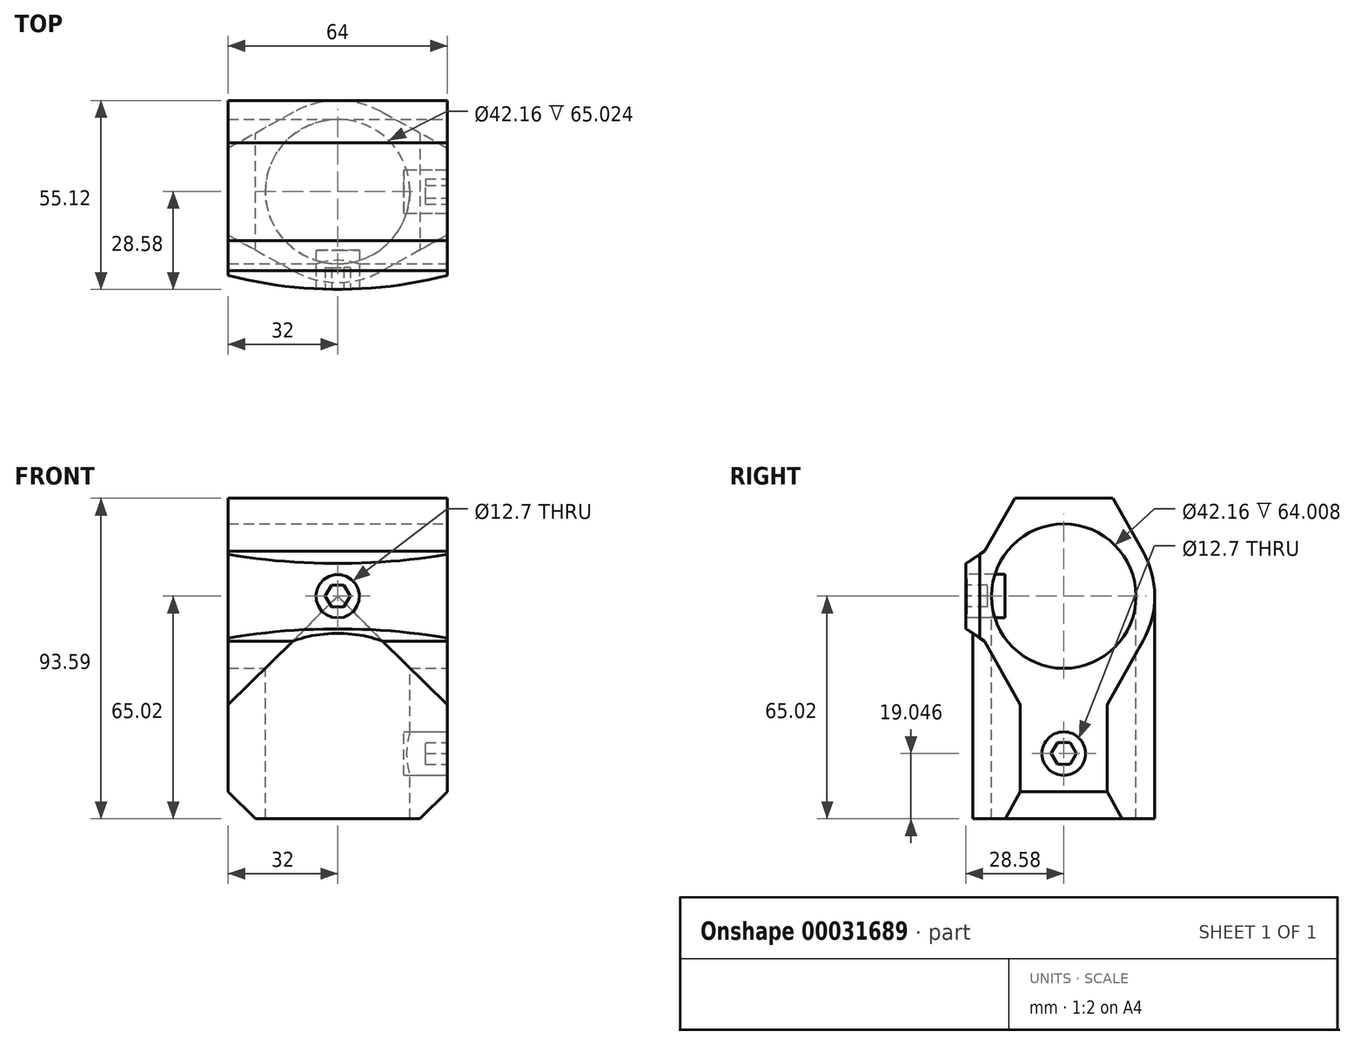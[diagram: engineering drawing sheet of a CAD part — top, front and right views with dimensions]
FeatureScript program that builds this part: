
annotation { "Feature Type Name" : "Feature", "Feature Type Description" : "" }
export const myFeature = defineFeature(function(context is Context, id is Id, definition is map)
    precondition{}
    {
        {
            var Q0;
            Q0=qCreatedBy(makeId("Top.planeOp"),FACE);
            var sketch = newSketch(context, id + "F0", { "sketchPlane" : qUnion([Q0])});
            skCircle(sketch, "E0", {"center": v(0, 0) * mm, "radius": 21.08 * mm});
            skCircle(sketch, "E1", {"center": v(0, 0) * mm, "radius": 26.54 * mm});
            skLineSegment(sketch, "E2.rect.bottom", {"start": v(-32, -12.7) * mm, "end": v(32, -12.7) * mm});
            skLineSegment(sketch, "E2.rect.top", {"start": v(-32, 12.7) * mm, "end": v(32, 12.7) * mm});
            skLineSegment(sketch, "E2.rect.left", {"start": v(-32, -12.7) * mm, "end": v(-32, 12.7) * mm});
            skLineSegment(sketch, "E2.rect.right", {"start": v(32, -12.7) * mm, "end": v(32, 12.7) * mm});
            skLineSegment(sketch, "E3", {"start": v(-32, -12.7) * mm, "end": v(-12.78, -23.26) * mm});
            skLineSegment(sketch, "E4", {"start": v(-32, 12.7) * mm, "end": v(-12.78, 23.26) * mm});
            skLineSegment(sketch, "E5", {"start": v(32, 12.7) * mm, "end": v(12.78, 23.26) * mm});
            skLineSegment(sketch, "E6", {"start": v(32, -12.7) * mm, "end": v(12.78, -23.26) * mm});
            skSolve(sketch);
        }
        {
            var Q0;
            {var subQ0=sQuery(id+"F0.wireOp",EDGE,"E2.rect.top");var subQ3=sQuery(id+"F0.wireOp",EDGE,"E0");var subQ4=makeQuery(id+"F0.imprint","INTERSECT",VERTEX,{"disambiguationData":[OD(0.0)],"derivedFrom":[subQ3,subQ0]});Q0=makeQuery(id+"F0.imprint","IMPRINT",FACE,{"disambiguationData":[TD([[makeQuery(id+"F0.imprint","IMPRINT",EDGE,{"disambiguationData":[TD([[subQ4,-1.0]])],"derivedFrom":subQ3}),-1.0]])]});}
            var Q1;
            {var subQ0=sQuery(id+"F0.wireOp",EDGE,"E3");Q1=makeQuery(id+"F0.imprint","IMPRINT",FACE,{"disambiguationData":[TD([[makeQuery(id+"F0.imprint","IMPRINT",EDGE,{"derivedFrom":subQ0}),1.0]])]});}
            var Q2;
            {var subQ0=sQuery(id+"F0.wireOp",EDGE,"E2.rect.bottom");var subQ3=sQuery(id+"F0.wireOp",EDGE,"E0");var subQ4=makeQuery(id+"F0.imprint","INTERSECT",VERTEX,{"disambiguationData":[OD(0.0)],"derivedFrom":[subQ3,subQ0]});Q2=makeQuery(id+"F0.imprint","IMPRINT",FACE,{"disambiguationData":[TD([[makeQuery(id+"F0.imprint","IMPRINT",EDGE,{"disambiguationData":[TD([[subQ4,-1.0]])],"derivedFrom":subQ3}),-1.0]])]});}
            var Q3;
            {var subQ0=sQuery(id+"F0.wireOp",EDGE,"E6");Q3=makeQuery(id+"F0.imprint","IMPRINT",FACE,{"disambiguationData":[TD([[makeQuery(id+"F0.imprint","IMPRINT",EDGE,{"derivedFrom":subQ0}),-1.0]])]});}
            var Q4;
            {var subQ0=sQuery(id+"F0.wireOp",EDGE,"E2.rect.right");Q4=makeQuery(id+"F0.imprint","IMPRINT",FACE,{"disambiguationData":[TD([[makeQuery(id+"F0.imprint","IMPRINT",EDGE,{"derivedFrom":subQ0}),1.0]])]});}
            var Q5;
            {var subQ0=sQuery(id+"F0.wireOp",EDGE,"E2.rect.top");var subQ3=sQuery(id+"F0.wireOp",EDGE,"E0");var subQ4=makeQuery(id+"F0.imprint","INTERSECT",VERTEX,{"disambiguationData":[OD(1.0)],"derivedFrom":[subQ3,subQ0]});Q5=makeQuery(id+"F0.imprint","IMPRINT",FACE,{"disambiguationData":[TD([[makeQuery(id+"F0.imprint","IMPRINT",EDGE,{"disambiguationData":[TD([[subQ4,1.0]])],"derivedFrom":subQ3}),-1.0]])]});}
            var Q6;
            {var subQ0=sQuery(id+"F0.wireOp",EDGE,"E5");Q6=makeQuery(id+"F0.imprint","IMPRINT",FACE,{"disambiguationData":[TD([[makeQuery(id+"F0.imprint","IMPRINT",EDGE,{"derivedFrom":subQ0}),1.0]])]});}
            var Q7;
            {var subQ0=sQuery(id+"F0.wireOp",EDGE,"E2.rect.top");var subQ3=sQuery(id+"F0.wireOp",EDGE,"E0");var subQ6=makeQuery(id+"F0.imprint","INTERSECT",VERTEX,{"disambiguationData":[OD(0.0)],"derivedFrom":[subQ3,subQ0]});Q7=makeQuery(id+"F0.imprint","IMPRINT",FACE,{"disambiguationData":[TD([[makeQuery(id+"F0.imprint","IMPRINT",EDGE,{"disambiguationData":[TD([[subQ6,1.0]])],"derivedFrom":subQ3}),-1.0]])]});}
            var Q8;
            {var subQ0=sQuery(id+"F0.wireOp",EDGE,"E4");Q8=makeQuery(id+"F0.imprint","IMPRINT",FACE,{"disambiguationData":[TD([[makeQuery(id+"F0.imprint","IMPRINT",EDGE,{"derivedFrom":subQ0}),-1.0]])]});}
            var Q9;
            {var subQ0=sQuery(id+"F0.wireOp",EDGE,"E2.rect.left");Q9=makeQuery(id+"F0.imprint","IMPRINT",FACE,{"disambiguationData":[TD([[makeQuery(id+"F0.imprint","IMPRINT",EDGE,{"derivedFrom":subQ0}),-1.0]])]});}
            var Q10;
            {var subQ0=sQuery(id+"F0.wireOp",EDGE,"E2.rect.top");var subQ1=sQuery(id+"F0.wireOp",EDGE,"E0");var subQ3=makeQuery(id+"F0.imprint","INTERSECT",VERTEX,{"disambiguationData":[OD(0.0)],"derivedFrom":[subQ1,subQ0]});Q10=makeQuery(id+"F0.imprint","IMPRINT",FACE,{"disambiguationData":[TD([[makeQuery(id+"F0.imprint","IMPRINT",EDGE,{"disambiguationData":[TD([[subQ3,1.0]])],"derivedFrom":subQ1}),1.0]])]});}
            var Q11;
            {var subQ1=sQuery(id+"F0.wireOp",EDGE,"E0");var subQ4=sQuery(id+"F0.wireOp",EDGE,"E2.rect.top");var subQ6=makeQuery(id+"F0.imprint","INTERSECT",VERTEX,{"disambiguationData":[OD(0.0)],"derivedFrom":[subQ1,subQ4]});Q11=makeQuery(id+"F0.imprint","IMPRINT",FACE,{"disambiguationData":[TD([[makeQuery(id+"F0.imprint","IMPRINT",EDGE,{"disambiguationData":[TD([[subQ6,-1.0]])],"derivedFrom":subQ1}),1.0]])]});}
            var Q12;
            {var subQ0=sQuery(id+"F0.wireOp",EDGE,"E2.rect.bottom");var subQ1=sQuery(id+"F0.wireOp",EDGE,"E0");var subQ3=makeQuery(id+"F0.imprint","INTERSECT",VERTEX,{"disambiguationData":[OD(0.0)],"derivedFrom":[subQ1,subQ0]});Q12=makeQuery(id+"F0.imprint","IMPRINT",FACE,{"disambiguationData":[TD([[makeQuery(id+"F0.imprint","IMPRINT",EDGE,{"disambiguationData":[TD([[subQ3,-1.0]])],"derivedFrom":subQ1}),1.0]])]});}
            extrude(context, id + "F1", {"entities" : qUnion([Q0, Q1, Q2, Q3, Q4, Q5, Q6, Q7, Q8, Q9, Q10, Q11, Q12]), "oppositeDirection" : true, "depth" : 65.02 * mm});
        }
        {
            var Q0;
            Q0=qCreatedBy(makeId("Right.planeOp"),FACE);
            var sketch = newSketch(context, id + "F2", { "sketchPlane" : qUnion([Q0])});
            skCircle(sketch, "E7", {"center": v(0, 0) * mm, "radius": 21.08 * mm});
            skCircle(sketch, "E8", {"center": v(0, 0) * mm, "radius": 26.54 * mm});
            skLineSegment(sketch, "E9", {"start": v(-12.7, -31.75) * mm, "end": v(12.7, -31.75) * mm});
            skLineSegment(sketch, "E10", {"start": v(12.7, -31.75) * mm, "end": v(23.19, -12.91) * mm});
            skLineSegment(sketch, "E11", {"start": v(-12.7, -31.75) * mm, "end": v(-23.19, -12.91) * mm});
            skLineSegment(sketch, "E12", {"start": v(0, 28.58) * mm, "end": v(-14.29, 28.58) * mm});
            skLineSegment(sketch, "E13", {"start": v(-14.29, 28.58) * mm, "end": v(-23.07, 13.12) * mm});
            skLineSegment(sketch, "E14.MirrorCS", {"start": v(0, 28.58) * mm, "end": v(14.29, 28.58) * mm});
            skLineSegment(sketch, "E15.MirrorCS", {"start": v(14.29, 28.58) * mm, "end": v(23.07, 13.12) * mm});
            skLineSegment(sketch, "E16", {"start": v(-28.58, 0) * mm, "end": v(-28.58, 9.52) * mm});
            skLineSegment(sketch, "E17", {"start": v(-28.58, 9.53) * mm, "end": v(-23.07, 13.12) * mm});
            skLineSegment(sketch, "E18.MirrorCS", {"start": v(-28.58, 0) * mm, "end": v(-28.58, -9.52) * mm});
            skLineSegment(sketch, "E19.MirrorCS", {"start": v(-28.58, -9.53) * mm, "end": v(-23.07, -13.12) * mm});
            skSolve(sketch);
        }
        {
            var Q0;
            Q0=makeQuery(id+"F2.imprint","IMPRINT",FACE,{"disambiguationData":[TD([[makeQuery(id+"F2.imprint","IMPRINT",EDGE,{"derivedFrom":sQuery(id+"F2.wireOp",EDGE,"E12")}),1.0]])]});
            var Q1;
            Q1=makeQuery(id+"F2.imprint","IMPRINT",FACE,{"disambiguationData":[TD([[makeQuery(id+"F2.imprint","IMPRINT",EDGE,{"derivedFrom":sQuery(id+"F2.wireOp",EDGE,"E7")}),-1.0]])]});
            var Q2;
            Q2=makeQuery(id+"F2.imprint","IMPRINT",FACE,{"disambiguationData":[TD([[makeQuery(id+"F2.imprint","IMPRINT",EDGE,{"derivedFrom":sQuery(id+"F2.wireOp",EDGE,"E9")}),1.0]])]});
            var Q3;
            Q3=makeQuery(id+"F2.imprint","IMPRINT",FACE,{"disambiguationData":[TD([[makeQuery(id+"F2.imprint","IMPRINT",EDGE,{"derivedFrom":sQuery(id+"F2.wireOp",EDGE,"E7")}),1.0]])]});
            var Q4;
            {var subQ1=sQuery(id+"F2.wireOp",EDGE,"E11");var subQ3=sQuery(id+"F2.wireOp",EDGE,"E8");var subQ5=makeQuery(id+"F2.imprint","INTERSECT",VERTEX,{"derivedFrom":[subQ3,subQ1]});Q4=makeQuery(id+"F2.imprint","IMPRINT",FACE,{"disambiguationData":[TD([[makeQuery(id+"F2.imprint","IMPRINT",EDGE,{"disambiguationData":[TD([[subQ5,-1.0]])],"derivedFrom":subQ3}),-1.0]])]});}
            var Q5;
            Q5=makeQuery(id+"F2.imprint","IMPRINT",FACE,{"disambiguationData":[TD([[makeQuery(id+"F2.imprint","IMPRINT",EDGE,{"derivedFrom":sQuery(id+"F2.wireOp",EDGE,"E16")}),-1.0]])]});
            var Q6;
            Q6=makeQuery(id+"F1.opExtrude","SWEPT_FACE",FACE,{"disambiguationData":[OSD([sQuery(id+"F0.wireOp",EDGE,"E2.rect.right")])]});
            var Q7;
            Q7=makeQuery(id+"F1.opExtrude","SWEPT_FACE",FACE,{"disambiguationData":[OSD([sQuery(id+"F0.wireOp",EDGE,"E2.rect.left")])]});
            extrude(context, id + "F3", {"entities" : qUnion([Q0, Q1, Q2, Q3, Q4, Q5]), "operationType" : NewBodyOperationType.ADD, "endBound" : BoundingType.UP_TO_SURFACE, "endBoundEntityFace" : qUnion([Q6]), "depth" : 25.4 * mm, "hasSecondDirection" : true, "secondDirectionBound" : SecondDirectionBoundingType.UP_TO_SURFACE, "secondDirectionOppositeDirection" : true, "secondDirectionBoundEntityFace" : qUnion([Q7]), "secondDirectionDepth" : 25.4 * mm});
        }
        {
            var Q0;
            Q0=makeQuery(id+"F2.imprint","IMPRINT",FACE,{"disambiguationData":[TD([[makeQuery(id+"F2.imprint","IMPRINT",EDGE,{"derivedFrom":sQuery(id+"F2.wireOp",EDGE,"E7")}),1.0]])]});
            extrude(context, id + "F4", {"entities" : qUnion([Q0]), "operationType" : NewBodyOperationType.REMOVE, "endBound" : BoundingType.THROUGH_ALL, "oppositeDirection" : true, "depth" : 25.4 * mm, "hasSecondDirection" : true, "secondDirectionBound" : SecondDirectionBoundingType.THROUGH_ALL, "secondDirectionOppositeDirection" : false, "secondDirectionDepth" : 25.4 * mm});
        }
        {
            var Q0;
            {var subQ0=sQuery(id+"F0.wireOp",EDGE,"E2.rect.bottom");var subQ1=sQuery(id+"F0.wireOp",EDGE,"E0");var subQ3=makeQuery(id+"F0.imprint","INTERSECT",VERTEX,{"disambiguationData":[OD(0.0)],"derivedFrom":[subQ1,subQ0]});Q0=makeQuery(id+"F0.imprint","IMPRINT",FACE,{"disambiguationData":[TD([[makeQuery(id+"F0.imprint","IMPRINT",EDGE,{"disambiguationData":[TD([[subQ3,-1.0]])],"derivedFrom":subQ1}),1.0]])]});}
            var Q1;
            {var subQ1=sQuery(id+"F0.wireOp",EDGE,"E0");var subQ4=sQuery(id+"F0.wireOp",EDGE,"E2.rect.top");var subQ6=makeQuery(id+"F0.imprint","INTERSECT",VERTEX,{"disambiguationData":[OD(0.0)],"derivedFrom":[subQ1,subQ4]});Q1=makeQuery(id+"F0.imprint","IMPRINT",FACE,{"disambiguationData":[TD([[makeQuery(id+"F0.imprint","IMPRINT",EDGE,{"disambiguationData":[TD([[subQ6,-1.0]])],"derivedFrom":subQ1}),1.0]])]});}
            var Q2;
            {var subQ0=sQuery(id+"F0.wireOp",EDGE,"E2.rect.top");var subQ1=sQuery(id+"F0.wireOp",EDGE,"E0");var subQ3=makeQuery(id+"F0.imprint","INTERSECT",VERTEX,{"disambiguationData":[OD(0.0)],"derivedFrom":[subQ1,subQ0]});Q2=makeQuery(id+"F0.imprint","IMPRINT",FACE,{"disambiguationData":[TD([[makeQuery(id+"F0.imprint","IMPRINT",EDGE,{"disambiguationData":[TD([[subQ3,1.0]])],"derivedFrom":subQ1}),1.0]])]});}
            extrude(context, id + "F5", {"entities" : qUnion([Q0, Q1, Q2]), "operationType" : NewBodyOperationType.REMOVE, "endBound" : BoundingType.THROUGH_ALL, "oppositeDirection" : true, "depth" : 25.4 * mm});
        }
        {
            var Q0;
            Q0=makeQuery(id+"F1.opExtrude","CAP_EDGE",EDGE,{"disambiguationData":[OSD([sQuery(id+"F0.wireOp",EDGE,"E2.rect.right")])],"isStart":false});
            var Q1;
            Q1=makeQuery(id+"F1.opExtrude","CAP_EDGE",EDGE,{"disambiguationData":[OSD([sQuery(id+"F0.wireOp",EDGE,"E2.rect.left")])],"isStart":false});
            chamfer(context, id + "F6", {"entities" : qUnion([Q0, Q1]), "width" : 7.94 * mm, "tangentPropagation" : true});
        }
        {
            var Q0;
            Q0=makeQuery(id+"F3.boolean.opBoolean","MERGE",FACE,{"derivedFrom":[makeQuery(id+"F1.opExtrude","SWEPT_FACE",FACE,{"disambiguationData":[OSD([sQuery(id+"F0.wireOp",EDGE,"E2.rect.right")])]}),makeQuery(id+"F3.opExtrude","CAP_FACE",FACE,{"disambiguationData":[OSD([sQuery(id+"F2.wireOp",EDGE,"E8"),sQuery(id+"F2.wireOp",EDGE,"E9"),sQuery(id+"F2.wireOp",EDGE,"E10"),sQuery(id+"F2.wireOp",EDGE,"E11"),sQuery(id+"F2.wireOp",EDGE,"E12"),sQuery(id+"F2.wireOp",EDGE,"E13"),sQuery(id+"F2.wireOp",EDGE,"E14.MirrorCS"),sQuery(id+"F2.wireOp",EDGE,"E15.MirrorCS"),sQuery(id+"F2.wireOp",EDGE,"E16"),sQuery(id+"F2.wireOp",EDGE,"E17"),sQuery(id+"F2.wireOp",EDGE,"E18.MirrorCS"),sQuery(id+"F2.wireOp",EDGE,"E19.MirrorCS")])],"isStart":false})]});
            var sketch = newSketch(context, id + "F7", { "sketchPlane" : qUnion([Q0])});
            skCircle(sketch, "E20", {"center": v(0, -45.97) * mm, "radius": 6.35 * mm});
            skCircle(sketch, "E21.cCircle", {"center": v(0, -45.97) * mm, "radius": 3.18 * mm, "construction": true});
            skLineSegment(sketch, "E21.0", {"start": v(-1.83, -42.8) * mm, "end": v(1.83, -42.8) * mm});
            skLineSegment(sketch, "E21.1", {"start": v(1.83, -42.8) * mm, "end": v(3.67, -45.97) * mm});
            skLineSegment(sketch, "E21.2", {"start": v(3.67, -45.97) * mm, "end": v(1.83, -49.15) * mm});
            skLineSegment(sketch, "E21.3", {"start": v(1.83, -49.15) * mm, "end": v(-1.83, -49.15) * mm});
            skLineSegment(sketch, "E21.4", {"start": v(-1.83, -49.15) * mm, "end": v(-3.67, -45.97) * mm});
            skLineSegment(sketch, "E21.5", {"start": v(-3.67, -45.97) * mm, "end": v(-1.83, -42.8) * mm});
            skPoint(sketch, "E21.0.midPoint", {"position": v(0, -42.8) * mm});
            skSolve(sketch);
        }
        {
            var Q0;
            Q0=makeQuery(id+"F7.imprint","IMPRINT",FACE,{"disambiguationData":[TD([[makeQuery(id+"F7.imprint","IMPRINT",EDGE,{"derivedFrom":sQuery(id+"F7.wireOp",EDGE,"E21.0")}),-1.0]])]});
            var Q1;
            Q1=makeQuery(id+"F7.imprint","IMPRINT",FACE,{"disambiguationData":[TD([[makeQuery(id+"F7.imprint","IMPRINT",EDGE,{"derivedFrom":sQuery(id+"F7.wireOp",EDGE,"E20")}),1.0]])]});
            extrude(context, id + "F8", {"entities" : qUnion([Q0, Q1]), "oppositeDirection" : true, "depth" : 12.7 * mm});
        }
        {
            var Q0;
            Q0=makeQuery(id+"F3.opExtrude","SWEPT_FACE",FACE,{"disambiguationData":[OSD([sQuery(id+"F2.wireOp",EDGE,"E16"),sQuery(id+"F2.wireOp",EDGE,"E18.MirrorCS")])]});
            var sketch = newSketch(context, id + "F9", { "sketchPlane" : qUnion([Q0])});
            skCircle(sketch, "E22", {"center": v(0, 0) * mm, "radius": 6.35 * mm});
            skCircle(sketch, "E23.cCircle", {"center": v(0, 0) * mm, "radius": 3.17 * mm, "construction": true});
            skLineSegment(sketch, "E23.0", {"start": v(-1.83, 3.17) * mm, "end": v(1.83, 3.17) * mm});
            skLineSegment(sketch, "E23.1", {"start": v(1.83, 3.18) * mm, "end": v(3.67, 0) * mm});
            skLineSegment(sketch, "E23.2", {"start": v(3.67, 0) * mm, "end": v(1.83, -3.18) * mm});
            skLineSegment(sketch, "E23.3", {"start": v(1.83, -3.17) * mm, "end": v(-1.83, -3.17) * mm});
            skLineSegment(sketch, "E23.4", {"start": v(-1.83, -3.18) * mm, "end": v(-3.67, 0) * mm});
            skLineSegment(sketch, "E23.5", {"start": v(-3.67, 0) * mm, "end": v(-1.83, 3.18) * mm});
            skPoint(sketch, "E23.0.midPoint", {"position": v(0, 3.17) * mm});
            skSolve(sketch);
        }
        {
            var Q0;
            Q0=makeQuery(id+"F9.imprint","IMPRINT",FACE,{"disambiguationData":[TD([[makeQuery(id+"F9.imprint","IMPRINT",EDGE,{"derivedFrom":sQuery(id+"F9.wireOp",EDGE,"E23.0")}),-1.0]])]});
            var Q1;
            Q1=makeQuery(id+"F9.imprint","IMPRINT",FACE,{"disambiguationData":[TD([[makeQuery(id+"F9.imprint","IMPRINT",EDGE,{"derivedFrom":sQuery(id+"F9.wireOp",EDGE,"E22")}),1.0]])]});
            extrude(context, id + "F10", {"entities" : qUnion([Q0, Q1]), "oppositeDirection" : true, "depth" : 11.43 * mm});
        }
        {
            var Q0;
            Q0=makeQuery(id+"F8.opExtrude","SWEPT_BODY",BODY,{"disambiguationData":[OSD([sQuery(id+"F7.wireOp",EDGE,"E20")])]});
            var Q1;
            Q1=makeQuery(id+"F10.opExtrude","SWEPT_BODY",BODY,{"disambiguationData":[OSD([sQuery(id+"F9.wireOp",EDGE,"E22")])]});
            var Q2;
            Q2=makeQuery(id+"F1.opExtrude","SWEPT_BODY",BODY,{"disambiguationData":[OSD([sQuery(id+"F0.wireOp",EDGE,"E1"),sQuery(id+"F0.wireOp",EDGE,"E2.rect.left"),sQuery(id+"F0.wireOp",EDGE,"E2.rect.right"),sQuery(id+"F0.wireOp",EDGE,"E3"),sQuery(id+"F0.wireOp",EDGE,"E4"),sQuery(id+"F0.wireOp",EDGE,"E5"),sQuery(id+"F0.wireOp",EDGE,"E6")])]});
            booleanBodies(context, id + "F11", {"operationType" : BooleanOperationType.SUBTRACTION, "tools" : qUnion([Q0, Q1]), "targets" : qUnion([Q2]), "keepTools" : true});
        }
        {
            var Q0;
            Q0=makeQuery(id+"F7.imprint","IMPRINT",FACE,{"disambiguationData":[TD([[makeQuery(id+"F7.imprint","IMPRINT",EDGE,{"derivedFrom":sQuery(id+"F7.wireOp",EDGE,"E21.0")}),-1.0]])]});
            extrude(context, id + "F12", {"entities" : qUnion([Q0]), "operationType" : NewBodyOperationType.REMOVE, "oppositeDirection" : true, "depth" : 6.35 * mm});
        }
        {
            var Q0;
            Q0=makeQuery(id+"F9.imprint","IMPRINT",FACE,{"disambiguationData":[TD([[makeQuery(id+"F9.imprint","IMPRINT",EDGE,{"derivedFrom":sQuery(id+"F9.wireOp",EDGE,"E23.0")}),-1.0]])]});
            extrude(context, id + "F13", {"entities" : qUnion([Q0]), "operationType" : NewBodyOperationType.REMOVE, "oppositeDirection" : true, "depth" : 6.35 * mm});
        }
        {
            var Q0;
            Q0=qCreatedBy(makeId("Top.planeOp"),FACE);
            var sketch = newSketch(context, id + "F14", { "sketchPlane" : qUnion([Q0])});
            skArc(sketch, "E24", {"start": v(-32, -24.48) * mm, "mid": v(0, -28.58) * mm, "end": v(32, -24.48) * mm});
            skLineSegment(sketch, "E25", {"start": v(-32, -24.48) * mm, "end": v(-32, -34.93) * mm});
            skLineSegment(sketch, "E26", {"start": v(-32, -34.93) * mm, "end": v(32, -34.92) * mm});
            skLineSegment(sketch, "E27", {"start": v(32, -34.92) * mm, "end": v(32, -24.48) * mm});
            skSolve(sketch);
        }
        {
            var Q0;
            Q0=makeQuery(id+"F14.imprint","IMPRINT",FACE,{"disambiguationData":[TD([[makeQuery(id+"F14.imprint","IMPRINT",EDGE,{"derivedFrom":sQuery(id+"F14.wireOp",EDGE,"E24")}),-1.0]])]});
            extrude(context, id + "F15", {"entities" : qUnion([Q0]), "operationType" : NewBodyOperationType.REMOVE, "endBound" : BoundingType.THROUGH_ALL, "oppositeDirection" : true, "depth" : 25.4 * mm, "hasSecondDirection" : true, "secondDirectionBound" : SecondDirectionBoundingType.THROUGH_ALL, "secondDirectionOppositeDirection" : false, "secondDirectionDepth" : 25.4 * mm});
        }
    });
